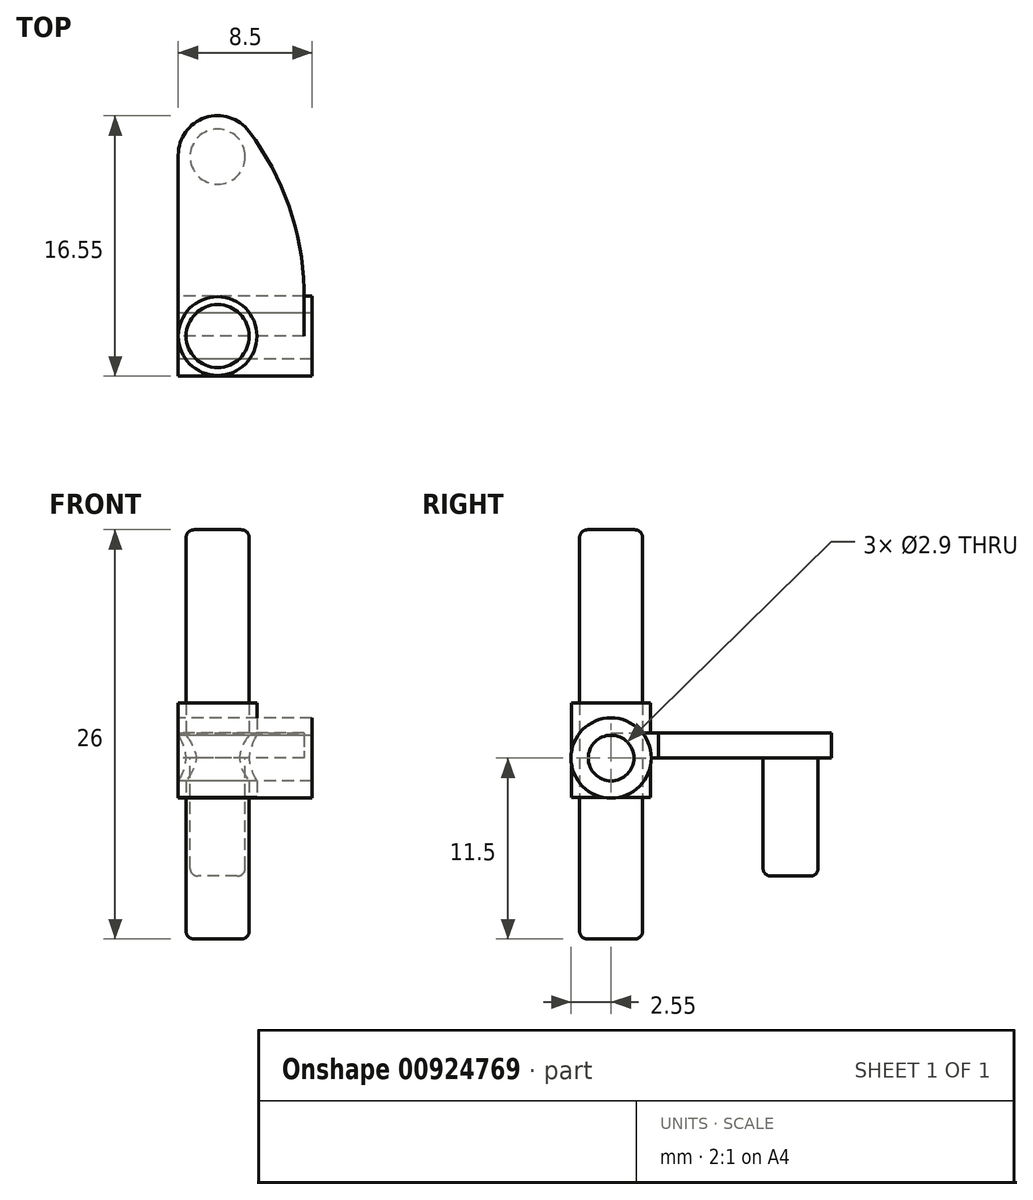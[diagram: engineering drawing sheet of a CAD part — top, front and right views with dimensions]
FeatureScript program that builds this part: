
annotation { "Feature Type Name" : "Feature", "Feature Type Description" : "" }
export const myFeature = defineFeature(function(context is Context, id is Id, definition is map)
    precondition{}
    {
        {
            var Q0;
            Q0=qCreatedBy(makeId("Right.planeOp"),FACE);
            var sketch = newSketch(context, id + "F0", { "sketchPlane" : qUnion([Q0])});
            skCircle(sketch, "E0", {"center": v(0, 0) * mm, "radius": 2.55 * mm});
            skSolve(sketch);
        }
        {
            var Q0;
            Q0=qSketchRegion(id+"F0",true);
            extrude(context, id + "F1", {"entities" : qUnion([Q0]), "depth" : 8.5 * mm, "offsetDistance" : 25.4 * mm});
        }
        {
            var Q0;
            Q0=qCreatedBy(makeId("Top.planeOp"),FACE);
            var sketch = newSketch(context, id + "F2", { "sketchPlane" : qUnion([Q0])});
            skLineSegment(sketch, "E1", {"start": v(0, 0) * mm, "end": v(0, 11.5) * mm});
            skArc(sketch, "E2", {"start": v(0, 11.5) * mm, "mid": v(1.7, 13.87) * mm, "end": v(4.5, 13) * mm});
            skLineSegment(sketch, "E3", {"start": v(0, 0) * mm, "end": v(8, 0) * mm});
            skLineSegment(sketch, "E4", {"start": v(8, 0) * mm, "end": v(8, 3) * mm});
            skArc(sketch, "E5", {"start": v(4.5, 13) * mm, "mid": v(7.02, 8.27) * mm, "end": v(8, 3) * mm});
            skSolve(sketch);
        }
        {
            var Q0;
            Q0=qSketchRegion(id+"F2",true);
            extrude(context, id + "F3", {"entities" : qUnion([Q0]), "depth" : 1.6 * mm, "offsetDistance" : 25.4 * mm});
        }
        {
            var Q0;
            Q0=qSketchRegion(id+"F2",true);
            extrude(context, id + "F4", {"entities" : qUnion([Q0]), "depth" : 1.6 * mm, "offsetDistance" : 25.4 * mm});
        }
        {
            var Q0;
            Q0=qCreatedBy(makeId("Top.planeOp"),FACE);
            var sketch = newSketch(context, id + "F5", { "sketchPlane" : qUnion([Q0])});
            skCircle(sketch, "E6", {"center": v(2.5, 11.4) * mm, "radius": 1.75 * mm});
            skSolve(sketch);
        }
        {
            var Q0;
            Q0=qSketchRegion(id+"F5",true);
            extrude(context, id + "F6", {"entities" : qUnion([Q0]), "oppositeDirection" : true, "depth" : 7.5 * mm, "offsetDistance" : 25.4 * mm});
        }
        {
            var Q0;
            Q0=qCreatedBy(makeId("Top.planeOp"),FACE);
            var sketch = newSketch(context, id + "F7", { "sketchPlane" : qUnion([Q0])});
            skCircle(sketch, "E7", {"center": v(2.5, 0) * mm, "radius": 2.5 * mm});
            skSolve(sketch);
        }
        {
            var Q0;
            Q0=qSketchRegion(id+"F7",true);
            extrude(context, id + "F8", {"entities" : qUnion([Q0]), "depth" : 3.5 * mm, "offsetDistance" : 25.4 * mm, "hasSecondDirection" : true, "secondDirectionOppositeDirection" : true, "secondDirectionDepth" : 2.5 * mm});
        }
        {
            var Q0;
            Q0=qCreatedBy(makeId("Top.planeOp"),FACE);
            var sketch = newSketch(context, id + "F9", { "sketchPlane" : qUnion([Q0])});
            skCircle(sketch, "E8", {"center": v(2.5, 0) * mm, "radius": 2 * mm});
            skSolve(sketch);
        }
        {
            var Q0;
            Q0=qSketchRegion(id+"F9",true);
            extrude(context, id + "F10", {"entities" : qUnion([Q0]), "depth" : 14.5 * mm, "offsetDistance" : 25.4 * mm, "hasSecondDirection" : true, "secondDirectionOppositeDirection" : true, "secondDirectionDepth" : 11.5 * mm});
        }
        {
            var Q0;
            Q0=sQuery(id+"F0.wireOp",VERTEX,"E0.center");
            var Q1;
            Q1=makeQuery(id+"F1.opExtrude","SWEPT_BODY",BODY,{"disambiguationData":[OSD([sQuery(id+"F0.wireOp",EDGE,"E0")])]});
            var Q2;
            Q2=makeQuery(id+"F3.opExtrude","SWEPT_BODY",BODY,{"disambiguationData":[OSD([sQuery(id+"F2.wireOp",EDGE,"E1"),sQuery(id+"F2.wireOp",EDGE,"E2"),sQuery(id+"F2.wireOp",EDGE,"E3"),sQuery(id+"F2.wireOp",EDGE,"E4"),sQuery(id+"F2.wireOp",EDGE,"E5")])]});
            var Q3;
            Q3=makeQuery(id+"F4.opExtrude","SWEPT_BODY",BODY,{"disambiguationData":[OSD([sQuery(id+"F2.wireOp",EDGE,"E1"),sQuery(id+"F2.wireOp",EDGE,"E2"),sQuery(id+"F2.wireOp",EDGE,"E3"),sQuery(id+"F2.wireOp",EDGE,"E4"),sQuery(id+"F2.wireOp",EDGE,"E5")])]});
            var Q4;
            Q4=makeQuery(id+"F8.opExtrude","SWEPT_BODY",BODY,{"disambiguationData":[OSD([sQuery(id+"F7.wireOp",EDGE,"E7")])]});
            var Q5;
            Q5=makeQuery(id+"F10.opExtrude","SWEPT_BODY",BODY,{"disambiguationData":[OSD([sQuery(id+"F9.wireOp",EDGE,"E8")])]});
            hole(context, id + "F11", {"style" : HoleStyle.SIMPLE, "endStyle" : HoleEndStyle.THROUGH, "oppositeDirection" : true, "holeDiameter" : 2.9 * mm, "majorDiameter" : 6.35 * mm, "isTappedThrough" : true, "tappedDepth" : 12.7 * mm, "tapClearance" : 3, "locations" : qUnion([Q0]), "scope" : qUnion([Q1, Q2, Q3, Q4, Q5])});
        }
        {
            var Q0;
            Q0=makeQuery(id+"F10.opExtrude","CAP_EDGE",EDGE,{"disambiguationData":[OSD([sQuery(id+"F9.wireOp",EDGE,"E8")])],"isStart":false});
            var Q1;
            Q1=makeQuery(id+"F10.opExtrude","CAP_EDGE",EDGE,{"disambiguationData":[OSD([sQuery(id+"F9.wireOp",EDGE,"E8")])],"isStart":true});
            var Q2;
            Q2=makeQuery(id+"F6.opExtrude","CAP_EDGE",EDGE,{"disambiguationData":[OSD([sQuery(id+"F5.wireOp",EDGE,"E6")])],"isStart":false});
            fillet(context, id + "F12", {"entities" : qUnion([Q0, Q1, Q2]), "radius" : 0.5 * mm, "tangentPropagation" : true, "allowEdgeOverflow" : false});
        }
    });
